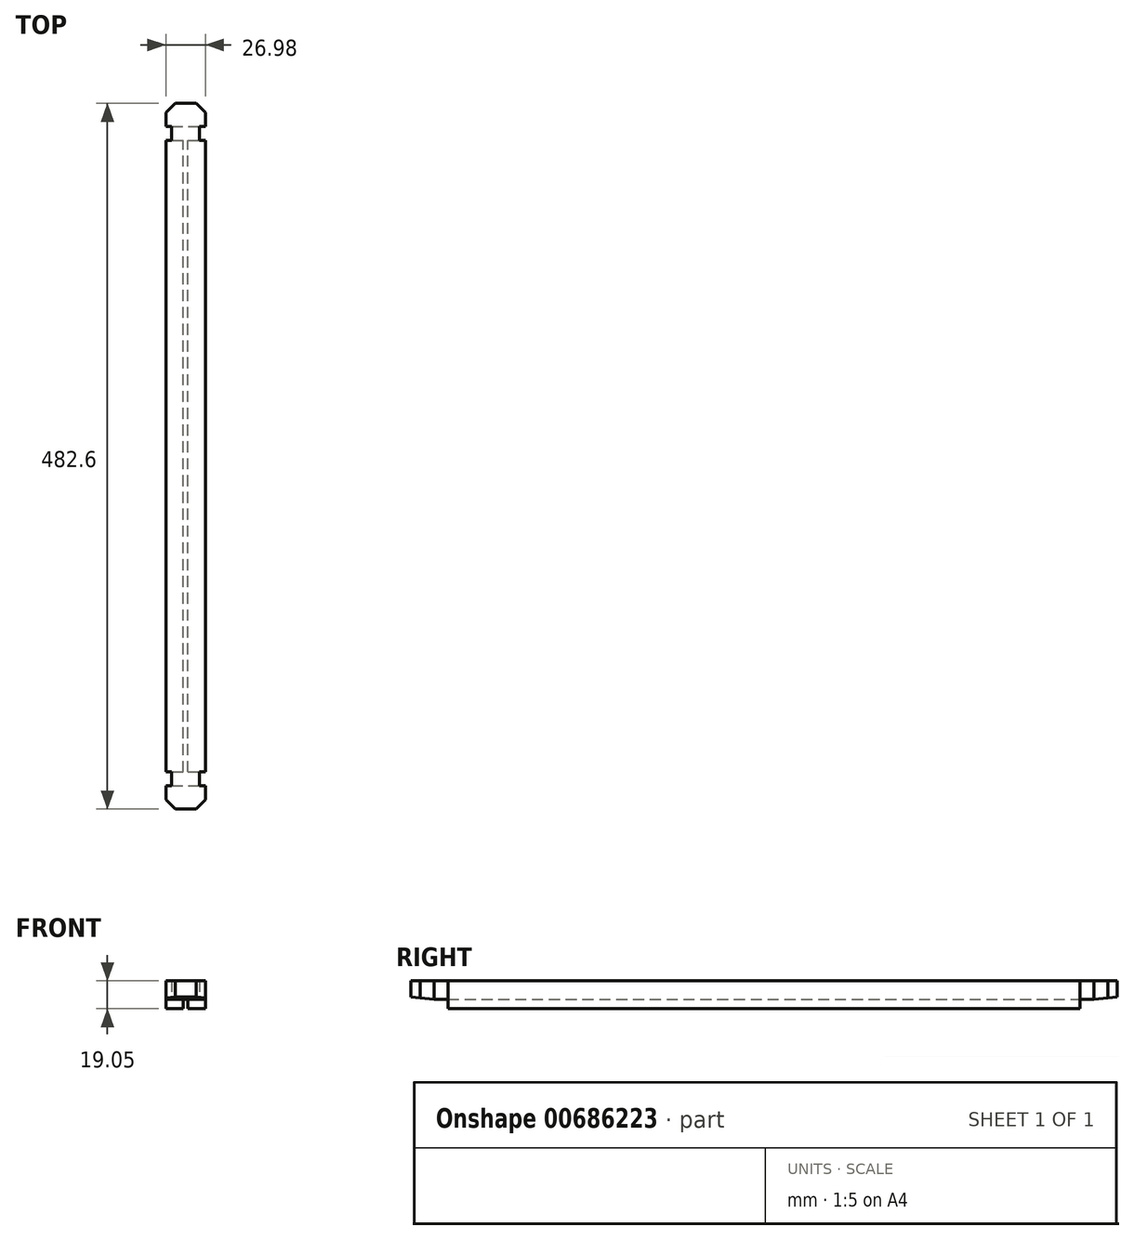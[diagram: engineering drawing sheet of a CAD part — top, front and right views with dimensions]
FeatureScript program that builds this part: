
annotation { "Feature Type Name" : "Feature", "Feature Type Description" : "" }
export const myFeature = defineFeature(function(context is Context, id is Id, definition is map)
    precondition{}
    {
        {
            var Q0;
            Q0=qCreatedBy(makeId("Front.planeOp"),FACE);
            var sketch = newSketch(context, id + "F0", { "sketchPlane" : qUnion([Q0])});
            skLineSegment(sketch, "E0", {"start": v(0, 46.49) * mm, "end": v(0, 0) * mm, "construction": true});
            skLineSegment(sketch, "E1", {"start": v(0, 0) * mm, "end": v(53.9, 0) * mm, "construction": true});
            skLineSegment(sketch, "E2", {"start": v(0, 19.05) * mm, "end": v(-13.5, 19.05) * mm});
            skLineSegment(sketch, "E3", {"start": v(-13.5, 19.05) * mm, "end": v(-13.5, 0) * mm});
            skLineSegment(sketch, "E4", {"start": v(-13.5, 0) * mm, "end": v(0, 0) * mm});
            skLineSegment(sketch, "E5", {"start": v(0, 19.05) * mm, "end": v(0, 0) * mm});
            skSolve(sketch);
        }
        {
            var Q0;
            Q0 = qSketchRegion(id + "F0", true);
            extrude(context, id + "F1", {"entities" : qUnion([Q0]), "depth" : 241.3 * mm, "offsetDistance" : 25.4 * mm});
        }
        {
            var Q0;
            Q0=qCreatedBy(makeId("Top.planeOp"),FACE);
            var sketch = newSketch(context, id + "F2", { "sketchPlane" : qUnion([Q0])});
            skLineSegment(sketch, "E6.bottom", {"start": v(-13.5, -215.9) * mm, "end": v(-9.52, -215.9) * mm});
            skLineSegment(sketch, "E6.top", {"start": v(-13.5, -225.43) * mm, "end": v(-9.52, -225.43) * mm});
            skLineSegment(sketch, "E6.left", {"start": v(-13.5, -215.9) * mm, "end": v(-13.5, -225.43) * mm});
            skLineSegment(sketch, "E6.right", {"start": v(-9.52, -215.9) * mm, "end": v(-9.52, -225.43) * mm});
            skSolve(sketch);
        }
        {
            var Q0;
            Q0 = qSketchRegion(id + "F2", true);
            extrude(context, id + "F3", {"entities" : qUnion([Q0]), "operationType" : NewBodyOperationType.REMOVE, "endBound" : BoundingType.THROUGH_ALL, "depth" : 25.4 * mm, "offsetDistance" : 25.4 * mm});
        }
        {
            var Q0;
            Q0=qCreatedBy(makeId("Right.planeOp"),FACE);
            var sketch = newSketch(context, id + "F4", { "sketchPlane" : qUnion([Q0])});
            skLineSegment(sketch, "E7", {"start": v(-215.9, 6.35) * mm, "end": v(-215.9, 0) * mm});
            skLineSegment(sketch, "E8", {"start": v(-215.9, 0) * mm, "end": v(-241.3, 0) * mm});
            skLineSegment(sketch, "E9", {"start": v(-241.3, 0) * mm, "end": v(-241.3, 7.94) * mm});
            skPoint(sketch, "E10", {"position": v(-225.43, 6.35) * mm});
            skLineSegment(sketch, "E11", {"start": v(-215.9, 6.35) * mm, "end": v(-225.43, 6.35) * mm});
            skLineSegment(sketch, "E12", {"start": v(-225.43, 6.35) * mm, "end": v(-241.3, 7.94) * mm});
            skLineSegment(sketch, "E13", {"start": v(-225.43, 6.35) * mm, "end": v(-225.43, 0) * mm, "construction": true});
            skSolve(sketch);
        }
        {
            var Q0;
            Q0 = qSketchRegion(id + "F4", true);
            extrude(context, id + "F5", {"entities" : qUnion([Q0]), "operationType" : NewBodyOperationType.REMOVE, "endBound" : BoundingType.THROUGH_ALL, "oppositeDirection" : true, "depth" : 25.4 * mm, "offsetDistance" : 25.4 * mm});
        }
        {
            var Q0;
            Q0=makeQuery(id+"F1.opExtrude","CAP_EDGE",EDGE,{"disambiguationData":[OSD([sQuery(id+"F0.wireOp",EDGE,"E3")])],"isStart":false});
            chamfer(context, id + "F6", {"entities" : qUnion([Q0]), "width" : 6.35 * mm, "tangentPropagation" : true});
        }
        {
            var Q0;
            Q0=makeQuery(id+"F1.opExtrude","SWEPT_BODY",BODY,{"disambiguationData":[OSD([sQuery(id+"F0.wireOp",EDGE,"E2"),sQuery(id+"F0.wireOp",EDGE,"E3"),sQuery(id+"F0.wireOp",EDGE,"E4"),sQuery(id+"F0.wireOp",EDGE,"E5")])]});
            var Q1;
            Q1=qCreatedBy(makeId("Right.planeOp"),FACE);
            mirror(context, id + "F7", {"operationType" : NewBodyOperationType.ADD, "entities" : qUnion([Q0]), "mirrorPlane" : qUnion([Q1])});
        }
        {
            var Q0;
            Q0=makeQuery(id+"F1.opExtrude","SWEPT_BODY",BODY,{"disambiguationData":[OSD([sQuery(id+"F0.wireOp",EDGE,"E2"),sQuery(id+"F0.wireOp",EDGE,"E3"),sQuery(id+"F0.wireOp",EDGE,"E4"),sQuery(id+"F0.wireOp",EDGE,"E5")])]});
            var Q1;
            Q1=qCreatedBy(makeId("Front.planeOp"),FACE);
            mirror(context, id + "F8", {"operationType" : NewBodyOperationType.ADD, "entities" : qUnion([Q0]), "mirrorPlane" : qUnion([Q1])});
        }
        {
            var Q0;
            {var subQ0=makeQuery(id+"F1.opExtrude","SWEPT_FACE",FACE,{"disambiguationData":[OSD([sQuery(id+"F0.wireOp",EDGE,"E4")])]});var subQ1=makeQuery(id+"F7.boolean.opBoolean","MERGE",FACE,{"derivedFrom":[subQ0,makeQuery(id+"F7.opPattern","COPY",FACE,{"derivedFrom":subQ0,"instanceName":"1"})]});Q0=makeQuery(id+"F8.boolean.opBoolean","MERGE",FACE,{"derivedFrom":[subQ1,makeQuery(id+"F8.opPattern","COPY",FACE,{"derivedFrom":subQ1,"instanceName":"1"})]});}
            var sketch = newSketch(context, id + "F9", { "sketchPlane" : qUnion([Q0])});
            skLineSegment(sketch, "E14.bottom", {"start": v(-1.59, 215.9) * mm, "end": v(1.59, 215.9) * mm});
            skLineSegment(sketch, "E14.top", {"start": v(-1.59, -215.9) * mm, "end": v(1.59, -215.9) * mm});
            skLineSegment(sketch, "E14.left", {"start": v(-1.59, 215.9) * mm, "end": v(-1.59, -215.9) * mm});
            skLineSegment(sketch, "E14.right", {"start": v(1.59, 215.9) * mm, "end": v(1.59, -215.9) * mm});
            skPoint(sketch, "E15", {"position": v(0, -215.9) * mm});
            skSolve(sketch);
        }
        {
            var Q0;
            Q0 = qSketchRegion(id + "F9", true);
            extrude(context, id + "F10", {"entities" : qUnion([Q0]), "operationType" : NewBodyOperationType.REMOVE, "oppositeDirection" : true, "depth" : 6.35 * mm, "offsetDistance" : 25.4 * mm});
        }
    });
